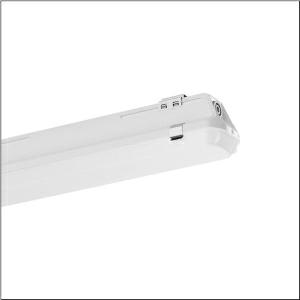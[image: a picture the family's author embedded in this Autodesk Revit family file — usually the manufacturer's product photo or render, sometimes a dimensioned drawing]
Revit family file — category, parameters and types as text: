
# Revit family: monsun_r__21_51fb10dp430b_6f0c
name_source: partatom
category: Lighting Fixtures
units: mm (PartAtom-declared; Revit-internal decimal feet)

## family parameters
Cut with Voids When Loaded = No
Host = Face
Light Source = No
Part Type = Normal
Room Calculation Point = No
Round Connector Dimension = Use Diameter
Shared = No

## types (1)
- --- (1 x LED, 3860 lm, 24.7 W, 4000K)
    Apparent Load = 25 VA
    CIE Flux Codes = 47 77 93 94 100
    Color Rendering = 80
    Color Temperature = 4000K
    Default Elevation = 1800 mm
    Description = Monsun® 21, damp-proof luminaire, chain hanger, primary optical cover: enclosure, of PMMA, light emission: direct distribution, primary light characteristic: symmetric, installation type: suspended mounting, surface-mounted, horizontal mounting, vertical mounting, LED, rated luminous flux: 3.860lm, luminous efficacy: 156lm/W, light colour: 840, colour temperature: 4000K, control gear: ECG DALI, with terminal, 5-pole, max. 2.5mm², mains connection: 220..240V, AC, 50/60Hz, rated input power: 25W, housing, of glass-fibre reinforced polyester, uncoated, bright grey, incl. chain hanger, length: 1.590mm, width: 90mm, height: 88mm, clip for enclosure, of stainless steel (V2A), ceiling mounting element, of stainless steel (V2A), chain hanger, of stainless steel (V2A), protection rating (complete): IP66, insulation class (complete): insulation class I (protective earthing), certification: CE, ENEC, VDE, UKCA, protection symbol: D, impact resistance: IK04, permissible operating ambient temperature: -25..+35°C, standard: EN 50419, EN 60598-2-1, corresponds to IFS (International Featured Standards) requirements for safety and quality in the food industry, for indoor or canopied outdoor use, no direct snow, no direct sun, no direct rain, contact your sales advisor before using the luminaires in applications with unclear chemical exposure, large temperature fluctuations or condensation-forming humidity, LABS conformity tested according to VDMA 24364:2018-05, packaging unit: 1 piece
    Height = 89 mm
    Lamp = 1 x LED
    Lamp Light Flux = 3860 lm
    Lamp Power = 24.7 W
    Lamp count = 1
    Length = 1590 mm
    Luminous efficacy = 156 lm/W
    Manufacturer = Siteco
    ModVariant = No
    Model = 51FB10DP430B
    Mounting Place = Ceiling
    Mounting Type = Surface mounted
    Number of Poles = 1
    OnlyDefault = Yes
    Power Factor = 1
    Product Name = Monsun® 21
    Product group = damp-proof luminaire
    ProductGroupID = 300
    Protection Class = Protection class I
    Protection Degree = IP 66
    RLX_Detail_Level = 1
    RLX_Emergency_Light_Flux = 0 lm
    RLX_Emergency_Type = 0
    RLX_Emergency_Type_DB = No
    RlxData = <blob elided: 91749 chars, md5=991a579b>
    Socket = socket
    Standby Power = 0 W
    System Light Flux = 3860 lm
    System Power = 25 W
    Type Comments = factory setting: luminous flux: 100 % | dim-lin: 254 | 162 mA
    Type Image = l_1006717.jpg
    URL = http://relux.com
    VarID = @adj_134549
    Voltage = 0 V
    Weight = 0.00 kg
    Width = 90 mm

## geometry (parser evidence)
native form markers: Blend x4, Sweep x13
no freeform markers — native parametric forms only
